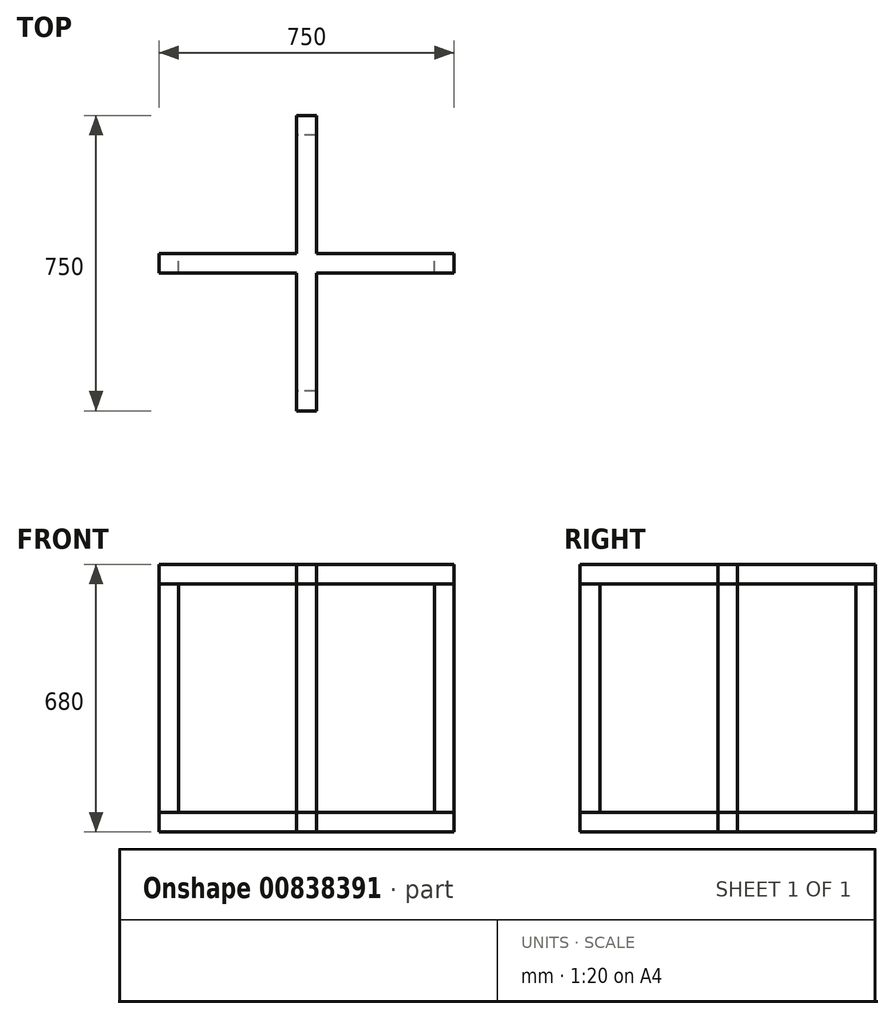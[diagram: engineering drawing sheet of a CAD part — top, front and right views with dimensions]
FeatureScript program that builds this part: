
annotation { "Feature Type Name" : "Feature", "Feature Type Description" : "" }
export const myFeature = defineFeature(function(context is Context, id is Id, definition is map)
    precondition{}
    {
        {
            var Q0;
            Q0=qCreatedBy(makeId("Top.planeOp"),FACE);
            var sketch = newSketch(context, id + "F0", { "sketchPlane" : qUnion([Q0])});
            skLineSegment(sketch, "E0.bottom", {"start": v(0, 0) * mm, "end": v(350, 0) * mm});
            skLineSegment(sketch, "E0.top", {"start": v(0, 50) * mm, "end": v(350, 50) * mm});
            skLineSegment(sketch, "E0.left", {"start": v(0, 0) * mm, "end": v(0, 50) * mm});
            skLineSegment(sketch, "E0.right", {"start": v(750, 0) * mm, "end": v(750, 50) * mm});
            skLineSegment(sketch, "E1.bottom", {"start": v(400, 400) * mm, "end": v(350, 400) * mm});
            skLineSegment(sketch, "E1.top", {"start": v(400, -350) * mm, "end": v(350, -350) * mm});
            skLineSegment(sketch, "E1.left", {"start": v(400, 400) * mm, "end": v(400, 50) * mm});
            skLineSegment(sketch, "E1.right", {"start": v(350, 400) * mm, "end": v(350, 50) * mm});
            skLineSegment(sketch, "E2.trimOffspring", {"start": v(400, 50) * mm, "end": v(750, 50) * mm});
            skLineSegment(sketch, "E3.trimOffspring", {"start": v(400, 0) * mm, "end": v(400, -350) * mm});
            skLineSegment(sketch, "E4.trimOffspring", {"start": v(350, 0) * mm, "end": v(350, -350) * mm});
            skLineSegment(sketch, "E5.trimOffspring", {"start": v(400, 0) * mm, "end": v(750, 0) * mm});
            skSolve(sketch);
        }
        {
            var Q0;
            Q0 = qSketchRegion(id + "F0", true);
            extrude(context, id + "F1", {"entities" : qUnion([Q0]), "depth" : 680 * mm, "offsetDistance" : 25 * mm});
        }
        {
            var Q0;
            Q0=makeQuery(id+"F1.opExtrude","SWEPT_FACE",FACE,{"disambiguationData":[OSD([sQuery(id+"F0.wireOp",EDGE,"E0.bottom")])]});
            var sketch = newSketch(context, id + "F2", { "sketchPlane" : qUnion([Q0])});
            skLineSegment(sketch, "E6", {"start": v(0, 680) * mm, "end": v(0, 630) * mm, "construction": true});
            skLineSegment(sketch, "E7.bottom", {"start": v(0, 630) * mm, "end": v(582.34, 630) * mm});
            skLineSegment(sketch, "E7.top", {"start": v(0, 50) * mm, "end": v(582.34, 50) * mm});
            skLineSegment(sketch, "E7.left", {"start": v(0, 630) * mm, "end": v(0, 50) * mm});
            skLineSegment(sketch, "E7.right", {"start": v(582.34, 630) * mm, "end": v(582.34, 50) * mm});
            skSolve(sketch);
        }
        {
            var Q0;
            Q0 = qSketchRegion(id + "F2", true);
            extrude(context, id + "F3", {"entities" : qUnion([Q0]), "operationType" : NewBodyOperationType.REMOVE, "endBound" : BoundingType.THROUGH_ALL, "oppositeDirection" : true, "depth" : 25 * mm, "offsetDistance" : 25 * mm});
        }
        {
            var Q0;
            Q0=makeQuery(id+"F3.boolean.opBoolean","COPY",FACE,{"derivedFrom":makeQuery(id+"F3.opExtrude","CAP_FACE",FACE,{"disambiguationData":[OSD([sQuery(id+"F2.wireOp",EDGE,"E7.bottom"),sQuery(id+"F2.wireOp",EDGE,"E7.top"),sQuery(id+"F2.wireOp",EDGE,"E7.left"),sQuery(id+"F2.wireOp",EDGE,"E7.right")])],"isStart":true})});
            var sketch = newSketch(context, id + "F4", { "sketchPlane" : qUnion([Q0])});
            skLineSegment(sketch, "E8.bottom", {"start": v(-400, 630) * mm, "end": v(-350, 630) * mm});
            skLineSegment(sketch, "E8.top", {"start": v(-400, 50) * mm, "end": v(-350, 50) * mm});
            skLineSegment(sketch, "E8.left", {"start": v(-400, 630) * mm, "end": v(-400, 50) * mm});
            skLineSegment(sketch, "E8.right", {"start": v(-350, 630) * mm, "end": v(-350, 50) * mm});
            skSolve(sketch);
        }
        {
            var Q0;
            Q0 = qSketchRegion(id + "F4", true);
            extrude(context, id + "F5", {"entities" : qUnion([Q0]), "operationType" : NewBodyOperationType.REMOVE, "endBound" : BoundingType.THROUGH_ALL, "oppositeDirection" : true, "depth" : 25 * mm, "offsetDistance" : 25 * mm});
        }
        {
            var Q0;
            Q0=makeQuery(id+"F3.boolean.opBoolean","COPY",FACE,{"derivedFrom":makeQuery(id+"F3.opExtrude","SWEPT_FACE",FACE,{"disambiguationData":[OSD([sQuery(id+"F2.wireOp",EDGE,"E7.right")])]})});
            var sketch = newSketch(context, id + "F6", { "sketchPlane" : qUnion([Q0])});
            skLineSegment(sketch, "E9.bottom", {"start": v(-50, 630) * mm, "end": v(0, 630) * mm});
            skLineSegment(sketch, "E9.top", {"start": v(-50, 50) * mm, "end": v(0, 50) * mm});
            skLineSegment(sketch, "E9.left", {"start": v(-50, 630) * mm, "end": v(-50, 50) * mm});
            skLineSegment(sketch, "E9.right", {"start": v(0, 630) * mm, "end": v(0, 50) * mm});
            skSolve(sketch);
        }
        {
            var Q0;
            Q0 = qSketchRegion(id + "F6", true);
            extrude(context, id + "F7", {"entities" : qUnion([Q0]), "operationType" : NewBodyOperationType.REMOVE, "endBound" : BoundingType.THROUGH_ALL, "oppositeDirection" : true, "depth" : 25 * mm, "offsetDistance" : 25 * mm});
        }
        {
            var Q0;
            Q0=makeQuery(id+"F7.boolean.opBoolean","MERGE",FACE,{"derivedFrom":[makeQuery(id+"F5.boolean.opBoolean","MERGE",FACE,{"derivedFrom":[makeQuery(id+"F3.boolean.opBoolean","COPY",FACE,{"derivedFrom":makeQuery(id+"F3.opExtrude","SWEPT_FACE",FACE,{"disambiguationData":[OSD([sQuery(id+"F2.wireOp",EDGE,"E7.top")])]})}),makeQuery(id+"F5.opExtrude","SWEPT_FACE",FACE,{"disambiguationData":[OSD([sQuery(id+"F4.wireOp",EDGE,"E8.top")])]})]}),makeQuery(id+"F7.opExtrude","SWEPT_FACE",FACE,{"disambiguationData":[OSD([sQuery(id+"F6.wireOp",EDGE,"E9.top")])]})]});
            var sketch = newSketch(context, id + "F8", { "sketchPlane" : qUnion([Q0])});
            skLineSegment(sketch, "E10.bottom", {"start": v(750, 50) * mm, "end": v(700, 50) * mm});
            skLineSegment(sketch, "E10.top", {"start": v(750, 0) * mm, "end": v(700, 0) * mm});
            skLineSegment(sketch, "E10.left", {"start": v(750, 50) * mm, "end": v(750, 0) * mm});
            skLineSegment(sketch, "E10.right", {"start": v(700, 50) * mm, "end": v(700, 0) * mm});
            skLineSegment(sketch, "E11.bottom", {"start": v(350, 400) * mm, "end": v(400, 400) * mm});
            skLineSegment(sketch, "E11.top", {"start": v(350, 350) * mm, "end": v(400, 350) * mm});
            skLineSegment(sketch, "E11.left", {"start": v(350, 400) * mm, "end": v(350, 350) * mm});
            skLineSegment(sketch, "E11.right", {"start": v(400, 400) * mm, "end": v(400, 350) * mm});
            skLineSegment(sketch, "E12.bottom", {"start": v(0, 50) * mm, "end": v(50, 50) * mm});
            skLineSegment(sketch, "E12.top", {"start": v(0, 0) * mm, "end": v(50, 0) * mm});
            skLineSegment(sketch, "E12.left", {"start": v(0, 50) * mm, "end": v(0, 0) * mm});
            skLineSegment(sketch, "E12.right", {"start": v(50, 50) * mm, "end": v(50, 0) * mm});
            skLineSegment(sketch, "E13.bottom", {"start": v(350, -350) * mm, "end": v(400, -350) * mm});
            skLineSegment(sketch, "E13.top", {"start": v(350, -300) * mm, "end": v(400, -300) * mm});
            skLineSegment(sketch, "E13.left", {"start": v(350, -350) * mm, "end": v(350, -300) * mm});
            skLineSegment(sketch, "E13.right", {"start": v(400, -350) * mm, "end": v(400, -300) * mm});
            skSolve(sketch);
        }
        {
            var Q0;
            Q0 = qSketchRegion(id + "F8", true);
            extrude(context, id + "F9", {"entities" : qUnion([Q0]), "endBound" : BoundingType.UP_TO_NEXT, "depth" : 25 * mm, "offsetDistance" : 25 * mm});
        }
    });
